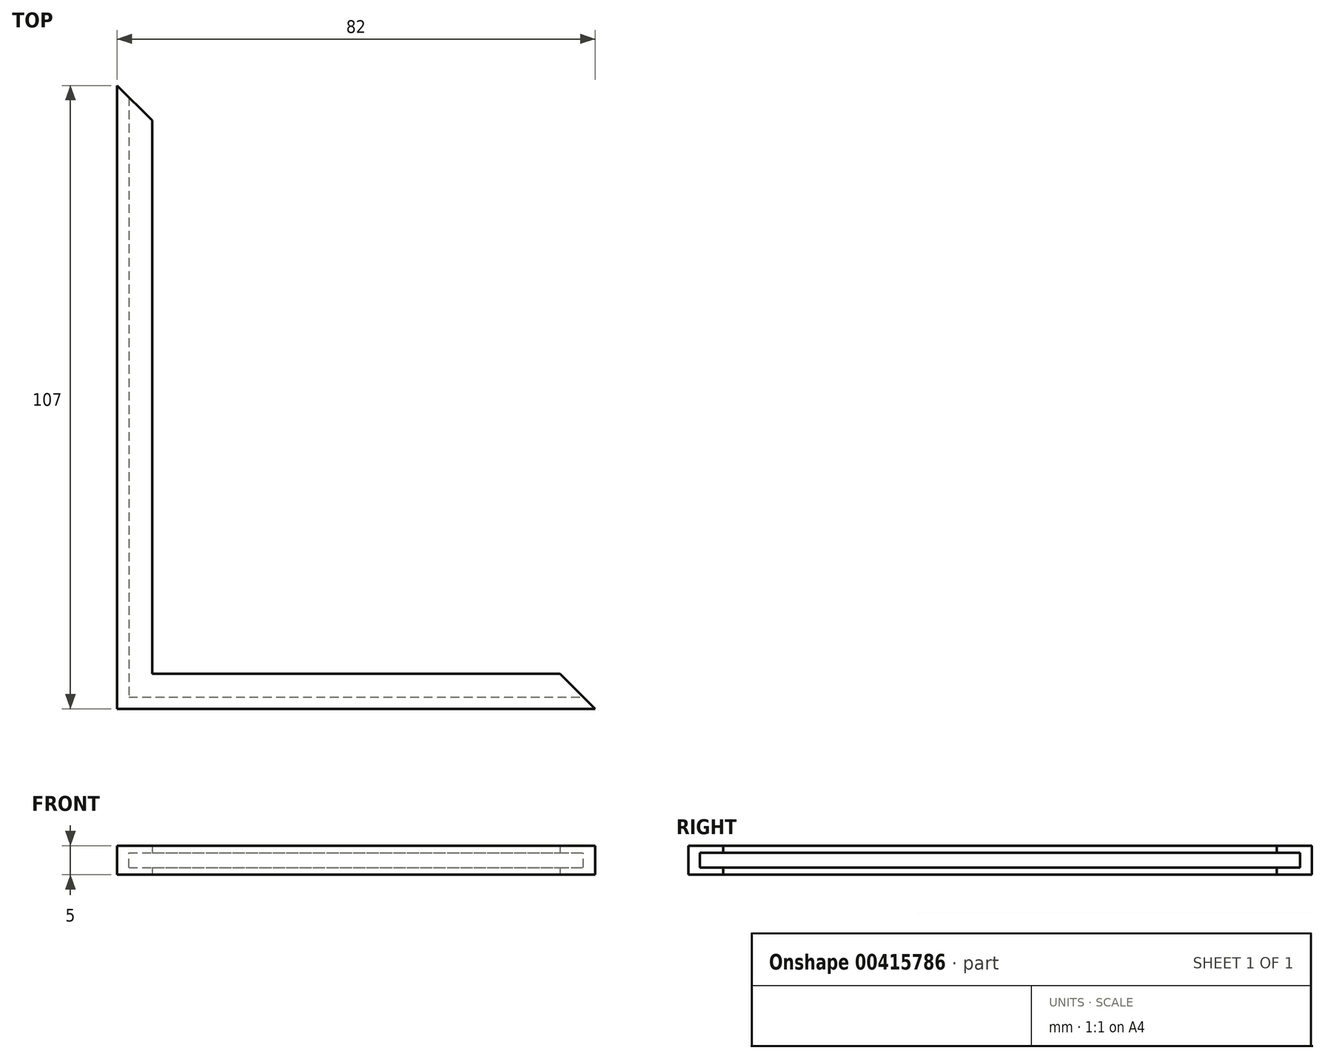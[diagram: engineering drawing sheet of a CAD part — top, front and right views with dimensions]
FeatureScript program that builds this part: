
annotation { "Feature Type Name" : "Feature", "Feature Type Description" : "" }
export const myFeature = defineFeature(function(context is Context, id is Id, definition is map)
    precondition{}
    {
        {
            var Q0;
            Q0=qCreatedBy(makeId("Top.planeOp"),FACE);
            var sketch = newSketch(context, id + "F0", { "sketchPlane" : qUnion([Q0])});
            skLineSegment(sketch, "E0", {"start": v(0, 0) * mm, "end": v(0, 107) * mm});
            skLineSegment(sketch, "E1", {"start": v(0, 107) * mm, "end": v(2, 105) * mm});
            skLineSegment(sketch, "E2", {"start": v(2, 105) * mm, "end": v(2, 2) * mm});
            skLineSegment(sketch, "E3", {"start": v(2, 2) * mm, "end": v(80, 2) * mm});
            skLineSegment(sketch, "E4", {"start": v(80, 2) * mm, "end": v(82, 0) * mm});
            skLineSegment(sketch, "E5", {"start": v(82, 0) * mm, "end": v(0, 0) * mm});
            skLineSegment(sketch, "E6", {"start": v(2, 105) * mm, "end": v(6, 101) * mm});
            skLineSegment(sketch, "E7", {"start": v(6, 101) * mm, "end": v(6, 6) * mm});
            skLineSegment(sketch, "E8", {"start": v(6, 6) * mm, "end": v(76, 6) * mm});
            skLineSegment(sketch, "E9", {"start": v(76, 6) * mm, "end": v(80, 2) * mm});
            skSolve(sketch);
        }
        {
            var Q0;
            Q0 = qSketchRegion(id + "F0", true);
            extrude(context, id + "F1", {"entities" : qUnion([Q0]), "depth" : 2.5 * mm, "hasSecondDirection" : true, "secondDirectionOppositeDirection" : true, "secondDirectionDepth" : 2.5 * mm});
        }
        {
            var Q0;
            Q0=makeQuery(id+"F0.imprint","IMPRINT",FACE,{"disambiguationData":[TD([[makeQuery(id+"F0.imprint","IMPRINT",EDGE,{"derivedFrom":sQuery(id+"F0.wireOp",EDGE,"E2")}),1.0]])]});
            extrude(context, id + "F2", {"entities" : qUnion([Q0]), "operationType" : NewBodyOperationType.REMOVE, "oppositeDirection" : true, "depth" : 1.25 * mm, "hasSecondDirection" : true, "secondDirectionOppositeDirection" : false, "secondDirectionDepth" : 1.25 * mm});
        }
    });
